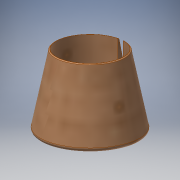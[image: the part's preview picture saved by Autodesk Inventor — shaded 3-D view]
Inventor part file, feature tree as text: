
AUTODESK INVENTOR PART (.ipt)
format: ipt  version: 2018 (Build 220112000, 112)  size: 181,760 bytes
history: native  units: mm
features: sketch x2, revolve x1, extrude x1
ambient origin geometry x8: Origin, YZ Plane, XZ Plane, XY Plane, X Axis, Y Axis, Z Axis, Center Point
bodies: Solid1 (feature_tree)
feature tree (4):
  revolve  "Revolution1"  [1 undecoded]
  extrude  "Extrusion1"  Depth=1.0mm
  sketch  "Sketch1"  dims[d0=11.0mm d1=2.094395mm]
  sketch  "Sketch2"  dims[d2=5.16mm d3=5.0mm d4=1.5mm d6=45.0deg d7=7.498122mm d8=0.5mm d9=0.15mm d10=90.0deg d11=1.0mm d12=6.39mm d13=10.0mm d14=0.0mm]
note: 1 required parameter value undecoded (feature->parameter linkage not recoverable at this tier; creation-order binding heuristic only, values carry confidence <= 0.55)
